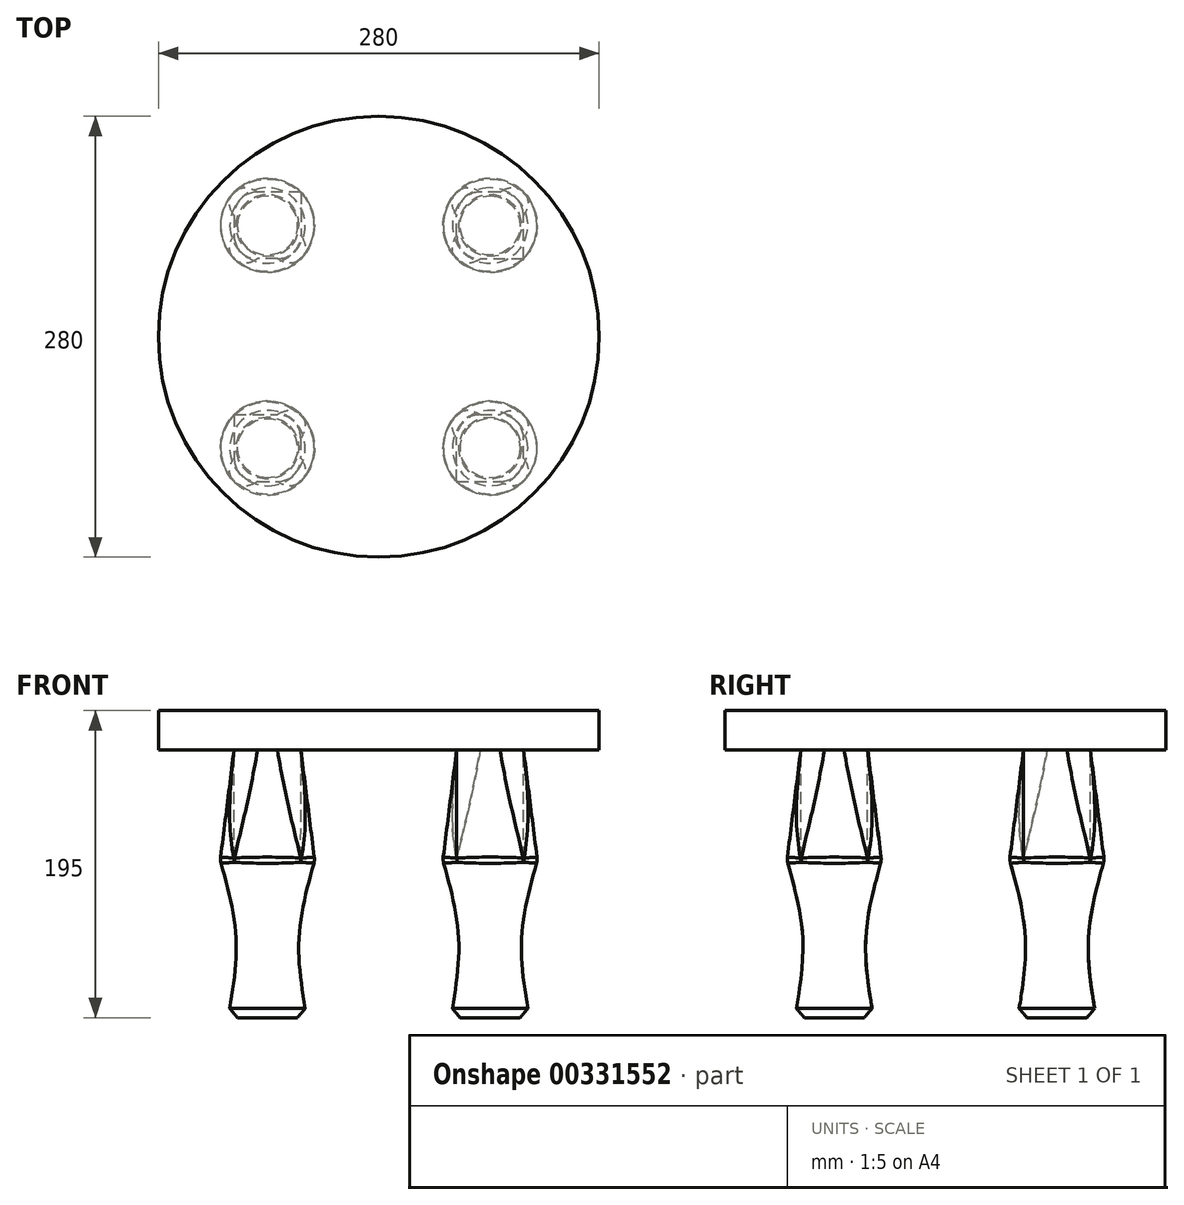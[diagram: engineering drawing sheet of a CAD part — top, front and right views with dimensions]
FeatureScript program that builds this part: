
annotation { "Feature Type Name" : "Feature", "Feature Type Description" : "" }
export const myFeature = defineFeature(function(context is Context, id is Id, definition is map)
    precondition{}
    {
        {
            var Q0;
            Q0=qCreatedBy(makeId("Top.planeOp"),FACE);
            cPlane(context, id + "F0", {"entities" : qUnion([Q0]), "cplaneType" : CPlaneType.OFFSET, "offset" : 50 * mm, "oppositeDirection" : true, "width" : 150 * mm, "height" : 150 * mm});
        }
        {
            var Q0;
            Q0=qCreatedBy(id+"F0.planeOp",FACE);
            cPlane(context, id + "F1", {"entities" : qUnion([Q0]), "cplaneType" : CPlaneType.OFFSET, "offset" : 50 * mm, "oppositeDirection" : true, "width" : 150 * mm, "height" : 150 * mm});
        }
        {
            var Q0;
            Q0=qCreatedBy(makeId("Top.planeOp"),FACE);
            var sketch = newSketch(context, id + "F2", { "sketchPlane" : qUnion([Q0])});
            skCircle(sketch, "E0", {"center": v(0, 0) * mm, "radius": 30 * mm});
            skSolve(sketch);
        }
        {
            var Q0;
            Q0=qCreatedBy(id+"F0.planeOp",FACE);
            var sketch = newSketch(context, id + "F3", { "sketchPlane" : qUnion([Q0])});
            skCircle(sketch, "E1", {"center": v(0, 0) * mm, "radius": 20 * mm});
            skSolve(sketch);
        }
        {
            var Q0;
            Q0=qCreatedBy(id+"F1.planeOp",FACE);
            var sketch = newSketch(context, id + "F4", { "sketchPlane" : qUnion([Q0])});
            skCircle(sketch, "E2", {"center": v(0, 0) * mm, "radius": 25 * mm});
            skSolve(sketch);
        }
        {
            var Q0;
            Q0=qSketchRegion(id+"F2",true);
            var Q1;
            Q1=qSketchRegion(id+"F3",true);
            var Q2;
            Q2=qSketchRegion(id+"F4",true);
            loft(context, id + "F5", {"sheetProfilesArray" : [{ "sheetProfileEntities" : qUnion([Q0]) }, { "sheetProfileEntities" : qUnion([Q1]) }, { "sheetProfileEntities" : qUnion([Q2]) }]});
        }
        {
            var Q0;
            Q0=qCreatedBy(makeId("Top.planeOp"),FACE);
            cPlane(context, id + "F6", {"entities" : qUnion([Q0]), "cplaneType" : CPlaneType.OFFSET, "offset" : 70 * mm, "width" : 150 * mm, "height" : 150 * mm});
        }
        {
            var Q0;
            Q0=qCreatedBy(id+"F6.planeOp",FACE);
            var sketch = newSketch(context, id + "F7", { "sketchPlane" : qUnion([Q0])});
            skLineSegment(sketch, "E3.bottom", {"start": v(-21.25, 21.18) * mm, "end": v(21.25, 21.18) * mm});
            skLineSegment(sketch, "E3.top", {"start": v(-21.25, -21.18) * mm, "end": v(21.25, -21.18) * mm});
            skLineSegment(sketch, "E3.left", {"start": v(-21.25, -21.18) * mm, "end": v(-21.25, 21.18) * mm});
            skLineSegment(sketch, "E3.right", {"start": v(21.25, -21.18) * mm, "end": v(21.25, 21.18) * mm});
            skSolve(sketch);
        }
        {
            var Q1;
            Q1=makeQuery(id+"F5.opLoft","CAP_FACE",FACE,{"disambiguationData":[OSD([makeQuery(id+"F2.imprint","IMPRINT",FACE,{"disambiguationData":[TD([[makeQuery(id+"F2.imprint","IMPRINT",EDGE,{"derivedFrom":sQuery(id+"F2.wireOp",EDGE,"E0")}),1.0]])]})])],"isStart":true});
            var Q2;
            Q2=makeQuery(id+"F7.imprint","IMPRINT",FACE,{"disambiguationData":[TD([[makeQuery(id+"F7.imprint","IMPRINT",EDGE,{"derivedFrom":sQuery(id+"F7.wireOp",EDGE,"E3.bottom")}),-1.0]])]});
            loft(context, id + "F8", {"operationType" : NewBodyOperationType.ADD, "sheetProfilesArray" : [{ "sheetProfileEntities" : qUnion([Q1]) }, { "sheetProfileEntities" : qUnion([Q2]) }]});
        }
        {
            var Q0;
            Q0=makeQuery(id+"F8.opLoft","SWEPT_EDGE",EDGE,{"disambiguationData":[OSD([sQuery(id+"F2.wireOp",EDGE,"E0"),sQuery(id+"F7.wireOp",EDGE,"E3.top"),sQuery(id+"F7.wireOp",EDGE,"E3.left"),sQuery(id+"F7.wireOp",EDGE,"E3.right")])]});
            var Q1;
            Q1=makeQuery(id+"F8.opLoft","SWEPT_EDGE",EDGE,{"disambiguationData":[OSD([sQuery(id+"F2.wireOp",EDGE,"E0"),sQuery(id+"F7.wireOp",EDGE,"E3.bottom"),sQuery(id+"F7.wireOp",EDGE,"E3.top"),sQuery(id+"F7.wireOp",EDGE,"E3.right")])]});
            var Q2;
            Q2=makeQuery(id+"F8.opLoft","SWEPT_EDGE",EDGE,{"disambiguationData":[OSD([sQuery(id+"F2.wireOp",EDGE,"E0"),sQuery(id+"F7.wireOp",EDGE,"E3.bottom"),sQuery(id+"F7.wireOp",EDGE,"E3.top"),sQuery(id+"F7.wireOp",EDGE,"E3.left")])]});
            var Q3;
            Q3=makeQuery(id+"F8.opLoft","SWEPT_EDGE",EDGE,{"disambiguationData":[OSD([sQuery(id+"F7.wireOp",EDGE,"E3.bottom"),sQuery(id+"F7.wireOp",EDGE,"E3.left")])]});
            fillet(context, id + "F9", {"entities" : qUnion([Q0, Q1, Q2, Q3]), "radius" : 15 * mm, "tangentPropagation" : true, "allowEdgeOverflow" : false});
        }
        {
            var Q0;
            {var subQ0=sQuery(id+"F2.wireOp",EDGE,"E0");Q0=makeQuery(id+"F8.boolean.opBoolean","MERGE",EDGE,{"derivedFrom":[makeQuery(id+"F5.opLoft","MID_CAP_EDGE",EDGE,{"disambiguationData":[OSD([subQ0])],"capPos":0.0}),makeQuery(id+"F8.opLoft","MID_CAP_EDGE",EDGE,{"disambiguationData":[OSD([subQ0,sQuery(id+"F7.wireOp",EDGE,"E3.bottom"),sQuery(id+"F7.wireOp",EDGE,"E3.left")])],"capPos":0.0})]});}
            fillet(context, id + "F10", {"entities" : qUnion([Q0]), "radius" : 10 * mm, "tangentPropagation" : true, "allowEdgeOverflow" : false});
        }
        {
            var Q0;
            Q0=makeQuery(id+"F5.opLoft","CAP_FACE",FACE,{"disambiguationData":[OSD([makeQuery(id+"F4.imprint","IMPRINT",FACE,{"disambiguationData":[TD([[makeQuery(id+"F4.imprint","IMPRINT",EDGE,{"derivedFrom":sQuery(id+"F4.wireOp",EDGE,"E2")}),1.0]])]})])],"isStart":true});
            chamfer(context, id + "F11", {"entities" : qUnion([Q0]), "width" : 5 * mm, "tangentPropagation" : true});
        }
        {
            var Q0;
            Q0=qCreatedBy(makeId("Top.planeOp"),FACE);
            var sketch = newSketch(context, id + "F12", { "sketchPlane" : qUnion([Q0])});
            skCircle(sketch, "E4", {"center": v(-70.71, 70.71) * mm, "radius": 100 * mm, "construction": true});
            skLineSegment(sketch, "E5", {"start": v(-70.71, 70.71) * mm, "end": v(58.04, 70.71) * mm, "construction": true});
            skLineSegment(sketch, "E6", {"start": v(-70.71, 70.71) * mm, "end": v(25.83, -25.83) * mm, "construction": true});
            skCircle(sketch, "E7", {"center": v(-320.71, 70.71) * mm, "radius": 250 * mm, "construction": true});
            skSolve(sketch);
        }
        {
            var Q0;
            Q0=qCreatedBy(makeId("Front.planeOp"),FACE);
            var Q1;
            Q1=sQuery(id+"F12.wireOp",VERTEX,"E5.start");
            cPlane(context, id + "F13", {"entities" : qUnion([Q0, Q1]), "cplaneType" : CPlaneType.PLANE_POINT, "offset" : 25 * mm, "width" : 150 * mm, "height" : 150 * mm});
        }
        {
            var Q0;
            Q0=qCreatedBy(id+"F13.planeOp",FACE);
            var sketch = newSketch(context, id + "F14", { "sketchPlane" : qUnion([Q0])});
            skLineSegment(sketch, "E8", {"start": v(-70.71, 0) * mm, "end": v(-70.71, 106.32) * mm});
            skLineSegment(sketch, "E9", {"start": v(-320.71, 0) * mm, "end": v(-320.71, 211.36) * mm});
            skSolve(sketch);
        }
        {
            var Q0;
            Q0=makeQuery(id+"F5.opLoft","SWEPT_BODY",BODY,{"disambiguationData":[OSD([makeQuery(id+"F2.imprint","IMPRINT",FACE,{"disambiguationData":[TD([[makeQuery(id+"F2.imprint","IMPRINT",EDGE,{"derivedFrom":sQuery(id+"F2.wireOp",EDGE,"E0")}),1.0]])]}),sQuery(id+"F3.wireOp",EDGE,"E1"),makeQuery(id+"F4.imprint","IMPRINT",FACE,{"disambiguationData":[TD([[makeQuery(id+"F4.imprint","IMPRINT",EDGE,{"derivedFrom":sQuery(id+"F4.wireOp",EDGE,"E2")}),1.0]])]})])]});
            var Q1;
            Q1=sQuery(id+"F14.wireOp",EDGE,"E8");
            circularPattern(context, id + "F15", {"entities" : qUnion([Q0]), "axis" : qUnion([Q1]), "angle" : 360 * degree, "instanceCount" : 4, "equalSpace" : true});
        }
        {
            var Q0;
            Q0=qCreatedBy(id+"F6.planeOp",FACE);
            var sketch = newSketch(context, id + "F16", { "sketchPlane" : qUnion([Q0])});
            skCircle(sketch, "E10", {"center": v(-70.71, 70.71) * mm, "radius": 140 * mm});
            skSolve(sketch);
        }
        {
            var Q0;
            Q0=makeQuery(id+"F16.imprint","IMPRINT",FACE,{"disambiguationData":[TD([[makeQuery(id+"F16.imprint","IMPRINT",EDGE,{"derivedFrom":sQuery(id+"F16.wireOp",EDGE,"E10")}),1.0]])]});
            extrude(context, id + "F17", {"entities" : qUnion([Q0]), "depth" : 25 * mm});
        }
    });
